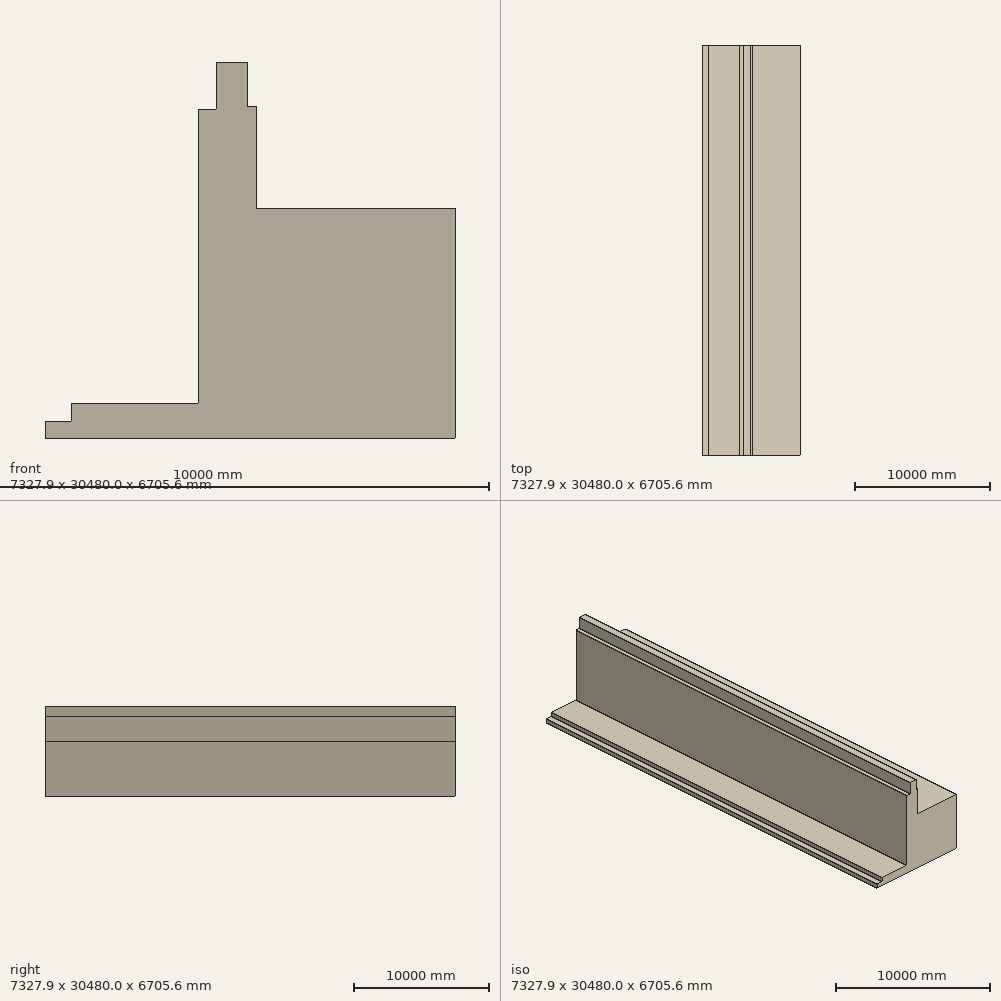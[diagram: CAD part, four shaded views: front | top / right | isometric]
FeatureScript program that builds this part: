
annotation { "Feature Type Name" : "Feature", "Feature Type Description" : "" }
export const myFeature = defineFeature(function(context is Context, id is Id, definition is map)
    precondition{}
    {
        {
            var Q0;
            Q0=qCreatedBy(makeId("Front.planeOp"),FACE);
            var sketch = newSketch(context, id + "F0", { "sketchPlane" : qUnion([Q0])});
            skLineSegment(sketch, "E0", {"start": v(863.6, 6096) * mm, "end": v(304.8, 6096) * mm});
            skLineSegment(sketch, "E1", {"start": v(304.8, 6096) * mm, "end": v(304.8, 5257.8) * mm});
            skLineSegment(sketch, "E2", {"start": v(0, 5257.8) * mm, "end": v(304.8, 5257.8) * mm});
            skLineSegment(sketch, "E3", {"start": v(0, 5257.8) * mm, "end": v(0, 0) * mm});
            skLineSegment(sketch, "E4", {"start": v(0, 0) * mm, "end": v(-2286, 0) * mm});
            skLineSegment(sketch, "E5", {"start": v(-2286, 0) * mm, "end": v(-2286, -304.8) * mm});
            skLineSegment(sketch, "E6", {"start": v(-2286, -304.8) * mm, "end": v(-2743.2, -304.8) * mm});
            skLineSegment(sketch, "E7", {"start": v(-2743.2, -304.8) * mm, "end": v(-2743.2, -609.6) * mm});
            skLineSegment(sketch, "E8", {"start": v(-2743.2, -609.6) * mm, "end": v(1022.35, -609.6) * mm});
            skLineSegment(sketch, "E9", {"start": v(863.6, 6096) * mm, "end": v(863.6, 5314.95) * mm});
            skLineSegment(sketch, "E10", {"start": v(863.6, 5314.95) * mm, "end": v(1022.35, 5314.95) * mm});
            skLineSegment(sketch, "E11", {"start": v(1022.35, 5314.95) * mm, "end": v(1022.35, 3486.15) * mm});
            skLineSegment(sketch, "E12", {"start": v(1022.35, 3486.15) * mm, "end": v(4584.73, 3486.15) * mm});
            skLineSegment(sketch, "E13", {"start": v(4584.73, 3486.15) * mm, "end": v(4584.73, -609.6) * mm});
            skLineSegment(sketch, "E14", {"start": v(4584.73, -609.6) * mm, "end": v(1022.35, -609.6) * mm});
            skSolve(sketch);
        }
        {
            var Q0;
            Q0=makeQuery(id+"F0.imprint","IMPRINT",FACE,{"disambiguationData":[TD([[makeQuery(id+"F0.imprint","IMPRINT",EDGE,{"derivedFrom":sQuery(id+"F0.wireOp",EDGE,"E0")}),1.0]])]});
            extrude(context, id + "F1", {"entities" : qUnion([Q0]), "endBound" : BoundingType.SYMMETRIC, "depth" : 30480 * mm});
        }
    });
